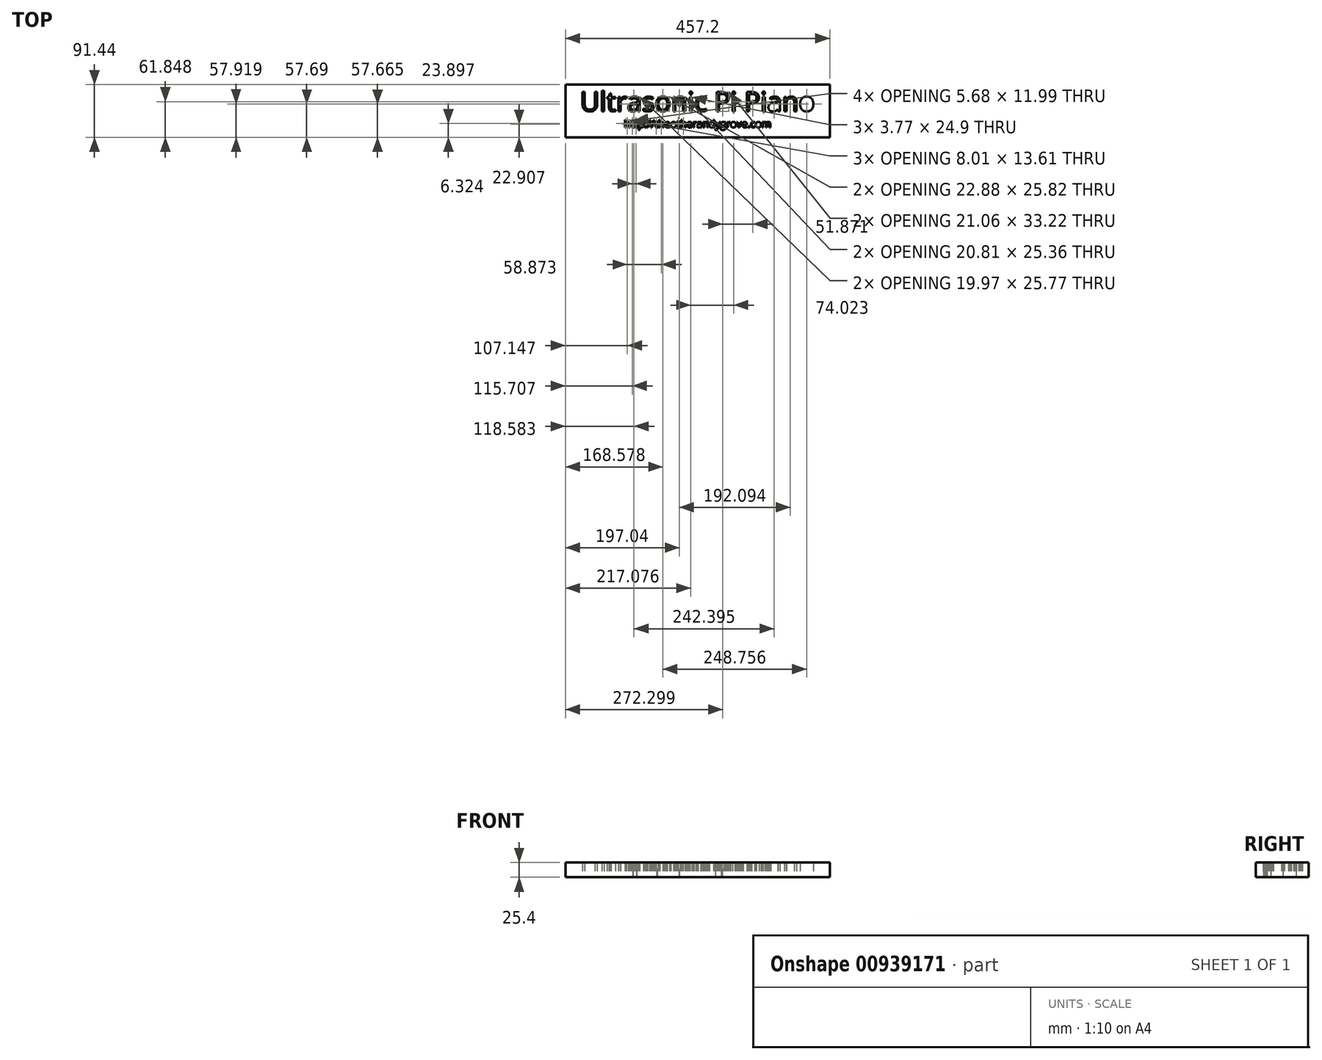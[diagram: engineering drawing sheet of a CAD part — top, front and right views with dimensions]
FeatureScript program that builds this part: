
annotation { "Feature Type Name" : "Feature", "Feature Type Description" : "" }
export const myFeature = defineFeature(function(context is Context, id is Id, definition is map)
    precondition{}
    {
        {
            var Q0;
            Q0=qCreatedBy(makeId("Top.planeOp"),FACE);
            var sketch = newSketch(context, id + "F0", { "sketchPlane" : qUnion([Q0])});
            skLineSegment(sketch, "E0.bottom", {"start": v(0, -127) * mm, "end": v(-457.2, -127) * mm});
            skLineSegment(sketch, "E0.top", {"start": v(0, -218.44) * mm, "end": v(-457.2, -218.44) * mm});
            skLineSegment(sketch, "E0.left", {"start": v(0, -127) * mm, "end": v(0, -218.44) * mm});
            skLineSegment(sketch, "E0.right", {"start": v(-457.2, -127) * mm, "end": v(-457.2, -218.44) * mm});
            skText(sketch, "E1", { "text": "Ultrasonic Pi Piano", "fontName": "OpenSans-Regular.ttf"});
            skText(sketch, "E2", { "text": "http://theotherandygrove.com", "fontName": "OpenSans-Regular.ttf"});
            const initialGuessF0  = {"E1": [-0.4318, -0.1732, 1, 0, 0.0335], "E2": [-0.3556, -0.20135, 1, 0, 0.0129]};
            skSetInitialGuess(sketch, initialGuessF0);
            skSolve(sketch);
        }
        {
            var Q0;
            Q0 = qSketchRegion(id + "F0", true);
            var Q1;
            Q1=makeQuery(id+"F0.imprint","IMPRINT",FACE,{"disambiguationData":[TD([[makeQuery(id+"F0.imprint","IMPRINT",EDGE,{"derivedFrom":sQuery(id+"F0.wireOp",EDGE,"E1.sketch_text.stroke-111")}),1.0]])]});
            var Q2;
            Q2=makeQuery(id+"F0.imprint","IMPRINT",FACE,{"disambiguationData":[TD([[makeQuery(id+"F0.imprint","IMPRINT",EDGE,{"derivedFrom":sQuery(id+"F0.wireOp",EDGE,"E1.sketch_text.stroke-69")}),1.0]])]});
            var Q3;
            Q3=makeQuery(id+"F0.imprint","IMPRINT",FACE,{"disambiguationData":[TD([[makeQuery(id+"F0.imprint","IMPRINT",EDGE,{"derivedFrom":sQuery(id+"F0.wireOp",EDGE,"E1.sketch_text.stroke-171")}),1.0]])]});
            var Q4;
            Q4=makeQuery(id+"F0.imprint","IMPRINT",FACE,{"disambiguationData":[TD([[makeQuery(id+"F0.imprint","IMPRINT",EDGE,{"derivedFrom":sQuery(id+"F0.wireOp",EDGE,"E1.sketch_text.stroke-198")}),1.0]])]});
            extrude(context, id + "F1", {"entities" : qUnion([Q0, Q1, Q2, Q3, Q4]), "depth" : 25.4 * mm, "offsetDistance" : 25.4 * mm});
        }
    });
